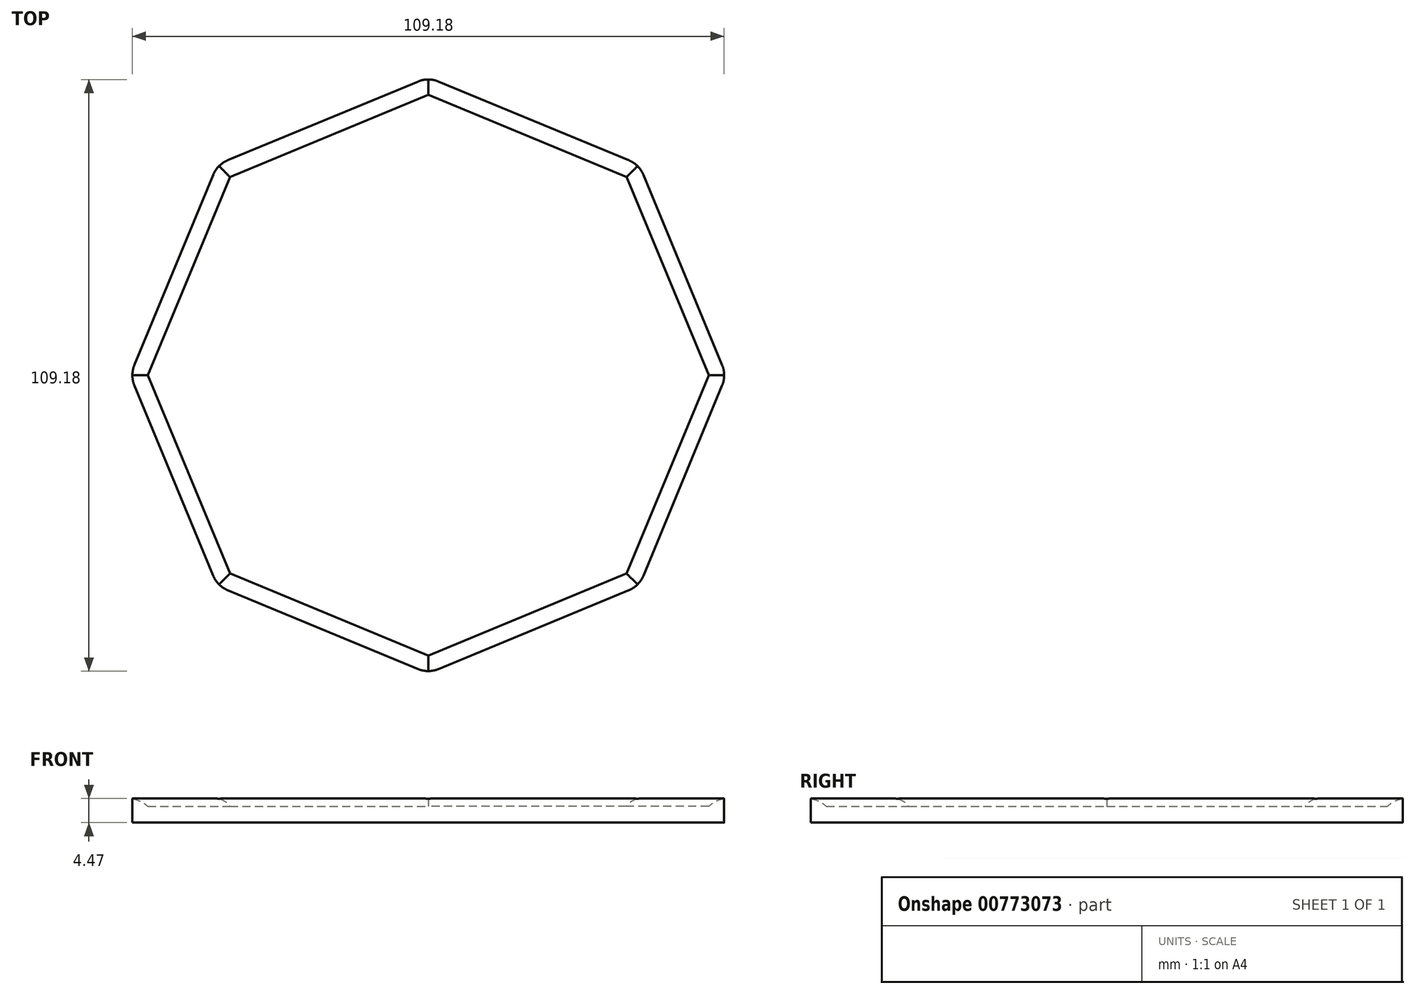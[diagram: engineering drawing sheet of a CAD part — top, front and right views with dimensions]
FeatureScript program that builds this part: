
annotation { "Feature Type Name" : "Feature", "Feature Type Description" : "" }
export const myFeature = defineFeature(function(context is Context, id is Id, definition is map)
    precondition{}
    {
        {
            var Q0;
            Q0=qCreatedBy(makeId("Top.planeOp"),FACE);
            var sketch = newSketch(context, id + "F0", { "sketchPlane" : qUnion([Q0])});
            skCircle(sketch, "E0.cCircle", {"center": v(0, 0) * mm, "radius": 55 * mm, "construction": true});
            skLineSegment(sketch, "E0.0", {"start": v(0, 55) * mm, "end": v(38.9, 38.9) * mm});
            skLineSegment(sketch, "E0.1", {"start": v(38.9, 38.9) * mm, "end": v(55, 0) * mm});
            skLineSegment(sketch, "E0.2", {"start": v(55, 0) * mm, "end": v(38.9, -38.9) * mm});
            skLineSegment(sketch, "E0.3", {"start": v(38.9, -38.9) * mm, "end": v(0, -55) * mm});
            skLineSegment(sketch, "E0.4", {"start": v(0, -55) * mm, "end": v(-38.9, -38.9) * mm});
            skLineSegment(sketch, "E0.5", {"start": v(-38.9, -38.9) * mm, "end": v(-55, 0) * mm});
            skLineSegment(sketch, "E0.6", {"start": v(-55, 0) * mm, "end": v(-38.9, 38.9) * mm});
            skLineSegment(sketch, "E0.7", {"start": v(-38.9, 38.9) * mm, "end": v(0, 55) * mm});
            skSolve(sketch);
        }
        {
            var Q0;
            Q0 = qSketchRegion(id + "F0", true);
            extrude(context, id + "F1", {"entities" : qUnion([Q0]), "depth" : 3 * mm, "offsetDistance" : 25 * mm});
        }
        {
            var Q0;
            Q0=makeQuery(id+"F1.opExtrude","CAP_FACE",FACE,{"disambiguationData":[OSD([sQuery(id+"F0.wireOp",EDGE,"E0.0"),sQuery(id+"F0.wireOp",EDGE,"E0.1"),sQuery(id+"F0.wireOp",EDGE,"E0.2"),sQuery(id+"F0.wireOp",EDGE,"E0.3"),sQuery(id+"F0.wireOp",EDGE,"E0.4"),sQuery(id+"F0.wireOp",EDGE,"E0.5"),sQuery(id+"F0.wireOp",EDGE,"E0.6"),sQuery(id+"F0.wireOp",EDGE,"E0.7")])],"isStart":false});
            var sketch = newSketch(context, id + "F2", { "sketchPlane" : qUnion([Q0])});
            skCircle(sketch, "E1.cCircle", {"center": v(0, 0) * mm, "radius": 51.74 * mm, "construction": true});
            skLineSegment(sketch, "E1.0", {"start": v(0, 51.74) * mm, "end": v(36.59, 36.59) * mm});
            skLineSegment(sketch, "E1.1", {"start": v(36.59, 36.59) * mm, "end": v(51.74, 0) * mm});
            skLineSegment(sketch, "E1.2", {"start": v(51.74, 0) * mm, "end": v(36.59, -36.59) * mm});
            skLineSegment(sketch, "E1.3", {"start": v(36.59, -36.59) * mm, "end": v(0, -51.74) * mm});
            skLineSegment(sketch, "E1.4", {"start": v(0, -51.74) * mm, "end": v(-36.59, -36.59) * mm});
            skLineSegment(sketch, "E1.5", {"start": v(-36.59, -36.59) * mm, "end": v(-51.74, 0) * mm});
            skLineSegment(sketch, "E1.6", {"start": v(-51.74, 0) * mm, "end": v(-36.59, 36.59) * mm});
            skLineSegment(sketch, "E1.7", {"start": v(-36.59, 36.59) * mm, "end": v(0, 51.74) * mm});
            skLineSegment(sketch, "E2.0", {"start": v(-38.9, 38.9) * mm, "end": v(0, 55) * mm});
            skLineSegment(sketch, "E3.0", {"start": v(38.9, 38.9) * mm, "end": v(55, 0) * mm});
            skLineSegment(sketch, "E4.0", {"start": v(55, 0) * mm, "end": v(38.9, -38.9) * mm});
            skLineSegment(sketch, "E5.0", {"start": v(38.9, -38.9) * mm, "end": v(0, -55) * mm});
            skLineSegment(sketch, "E6.0", {"start": v(0, -55) * mm, "end": v(-38.9, -38.9) * mm});
            skLineSegment(sketch, "E7.0.0", {"start": v(0, 55) * mm, "end": v(-38.9, 38.9) * mm});
            skLineSegment(sketch, "E7.0.1", {"start": v(-38.9, 38.9) * mm, "end": v(-55, 0) * mm});
            skLineSegment(sketch, "E7.0.2", {"start": v(-55, 0) * mm, "end": v(-38.9, -38.9) * mm});
            skLineSegment(sketch, "E7.0.3", {"start": v(-38.9, -38.9) * mm, "end": v(0, -55) * mm});
            skLineSegment(sketch, "E7.0.4", {"start": v(0, -55) * mm, "end": v(38.9, -38.9) * mm});
            skLineSegment(sketch, "E7.0.5", {"start": v(38.9, -38.9) * mm, "end": v(55, 0) * mm});
            skLineSegment(sketch, "E7.0.6", {"start": v(55, 0) * mm, "end": v(38.9, 38.9) * mm});
            skLineSegment(sketch, "E7.0.7", {"start": v(38.9, 38.9) * mm, "end": v(0, 55) * mm});
            skSolve(sketch);
        }
        {
            var Q0;
            Q0 = qSketchRegion(id + "F2", true);
            extrude(context, id + "F3", {"entities" : qUnion([Q0]), "operationType" : NewBodyOperationType.ADD, "depth" : 1.5 * mm, "offsetDistance" : 25 * mm});
        }
        {
            var Q0;
            Q0=makeQuery(id+"F3.opExtrude","CAP_EDGE",EDGE,{"disambiguationData":[OSD([sQuery(id+"F2.wireOp",EDGE,"E1.7")])],"isStart":false});
            var Q1;
            Q1=makeQuery(id+"F3.opExtrude","CAP_EDGE",EDGE,{"disambiguationData":[OSD([sQuery(id+"F2.wireOp",EDGE,"E1.6")])],"isStart":false});
            var Q2;
            Q2=makeQuery(id+"F3.opExtrude","CAP_EDGE",EDGE,{"disambiguationData":[OSD([sQuery(id+"F2.wireOp",EDGE,"E1.0")])],"isStart":false});
            var Q3;
            Q3=makeQuery(id+"F3.opExtrude","CAP_EDGE",EDGE,{"disambiguationData":[OSD([sQuery(id+"F2.wireOp",EDGE,"E1.1")])],"isStart":false});
            var Q4;
            Q4=makeQuery(id+"F3.opExtrude","CAP_EDGE",EDGE,{"disambiguationData":[OSD([sQuery(id+"F2.wireOp",EDGE,"E1.2")])],"isStart":false});
            var Q5;
            Q5=makeQuery(id+"F3.opExtrude","CAP_EDGE",EDGE,{"disambiguationData":[OSD([sQuery(id+"F2.wireOp",EDGE,"E1.3")])],"isStart":false});
            var Q6;
            Q6=makeQuery(id+"F3.opExtrude","CAP_EDGE",EDGE,{"disambiguationData":[OSD([sQuery(id+"F2.wireOp",EDGE,"E1.5")])],"isStart":false});
            var Q7;
            Q7=makeQuery(id+"F3.opExtrude","CAP_EDGE",EDGE,{"disambiguationData":[OSD([sQuery(id+"F2.wireOp",EDGE,"E1.4")])],"isStart":false});
            var Q8;
            Q8=makeQuery(id+"F3.boolean.opBoolean","MERGE",EDGE,{"derivedFrom":[makeQuery(id+"F1.opExtrude","SWEPT_EDGE",EDGE,{"disambiguationData":[OSD([sQuery(id+"F0.wireOp",EDGE,"E0.3"),sQuery(id+"F0.wireOp",EDGE,"E0.4")])]}),makeQuery(id+"F3.opExtrude","SWEPT_EDGE",EDGE,{"disambiguationData":[OSD([sQuery(id+"F2.wireOp",EDGE,"E7.0.3"),sQuery(id+"F2.wireOp",EDGE,"E7.0.4")])]})]});
            var Q9;
            Q9=makeQuery(id+"F3.boolean.opBoolean","MERGE",EDGE,{"derivedFrom":[makeQuery(id+"F1.opExtrude","SWEPT_EDGE",EDGE,{"disambiguationData":[OSD([sQuery(id+"F0.wireOp",EDGE,"E0.2"),sQuery(id+"F0.wireOp",EDGE,"E0.3")])]}),makeQuery(id+"F3.opExtrude","SWEPT_EDGE",EDGE,{"disambiguationData":[OSD([sQuery(id+"F2.wireOp",EDGE,"E7.0.4"),sQuery(id+"F2.wireOp",EDGE,"E7.0.5")])]})]});
            var Q10;
            Q10=makeQuery(id+"F3.boolean.opBoolean","MERGE",EDGE,{"derivedFrom":[makeQuery(id+"F1.opExtrude","SWEPT_EDGE",EDGE,{"disambiguationData":[OSD([sQuery(id+"F0.wireOp",EDGE,"E0.4"),sQuery(id+"F0.wireOp",EDGE,"E0.5")])]}),makeQuery(id+"F3.opExtrude","SWEPT_EDGE",EDGE,{"disambiguationData":[OSD([sQuery(id+"F2.wireOp",EDGE,"E7.0.2"),sQuery(id+"F2.wireOp",EDGE,"E7.0.3")])]})]});
            var Q11;
            Q11=makeQuery(id+"F3.boolean.opBoolean","MERGE",EDGE,{"derivedFrom":[makeQuery(id+"F1.opExtrude","SWEPT_EDGE",EDGE,{"disambiguationData":[OSD([sQuery(id+"F0.wireOp",EDGE,"E0.5"),sQuery(id+"F0.wireOp",EDGE,"E0.6")])]}),makeQuery(id+"F3.opExtrude","SWEPT_EDGE",EDGE,{"disambiguationData":[OSD([sQuery(id+"F2.wireOp",EDGE,"E7.0.1"),sQuery(id+"F2.wireOp",EDGE,"E7.0.2")])]})]});
            var Q12;
            Q12=makeQuery(id+"F3.boolean.opBoolean","MERGE",EDGE,{"derivedFrom":[makeQuery(id+"F1.opExtrude","SWEPT_EDGE",EDGE,{"disambiguationData":[OSD([sQuery(id+"F0.wireOp",EDGE,"E0.1"),sQuery(id+"F0.wireOp",EDGE,"E0.2")])]}),makeQuery(id+"F3.opExtrude","SWEPT_EDGE",EDGE,{"disambiguationData":[OSD([sQuery(id+"F2.wireOp",EDGE,"E7.0.5"),sQuery(id+"F2.wireOp",EDGE,"E7.0.6")])]})]});
            var Q13;
            Q13=makeQuery(id+"F3.boolean.opBoolean","MERGE",EDGE,{"derivedFrom":[makeQuery(id+"F1.opExtrude","SWEPT_EDGE",EDGE,{"disambiguationData":[OSD([sQuery(id+"F0.wireOp",EDGE,"E0.0"),sQuery(id+"F0.wireOp",EDGE,"E0.1")])]}),makeQuery(id+"F3.opExtrude","SWEPT_EDGE",EDGE,{"disambiguationData":[OSD([sQuery(id+"F2.wireOp",EDGE,"E7.0.6"),sQuery(id+"F2.wireOp",EDGE,"E7.0.7")])]})]});
            var Q14;
            Q14=makeQuery(id+"F3.boolean.opBoolean","MERGE",EDGE,{"derivedFrom":[makeQuery(id+"F1.opExtrude","SWEPT_EDGE",EDGE,{"disambiguationData":[OSD([sQuery(id+"F0.wireOp",EDGE,"E0.0"),sQuery(id+"F0.wireOp",EDGE,"E0.7")])]}),makeQuery(id+"F3.opExtrude","SWEPT_EDGE",EDGE,{"disambiguationData":[OSD([sQuery(id+"F2.wireOp",EDGE,"E7.0.0"),sQuery(id+"F2.wireOp",EDGE,"E7.0.7")])]})]});
            var Q15;
            Q15=makeQuery(id+"F3.boolean.opBoolean","MERGE",EDGE,{"derivedFrom":[makeQuery(id+"F1.opExtrude","SWEPT_EDGE",EDGE,{"disambiguationData":[OSD([sQuery(id+"F0.wireOp",EDGE,"E0.6"),sQuery(id+"F0.wireOp",EDGE,"E0.7")])]}),makeQuery(id+"F3.opExtrude","SWEPT_EDGE",EDGE,{"disambiguationData":[OSD([sQuery(id+"F2.wireOp",EDGE,"E7.0.0"),sQuery(id+"F2.wireOp",EDGE,"E7.0.1")])]})]});
            fillet(context, id + "F4", {"entities" : qUnion([Q0, Q1, Q2, Q3, Q4, Q5, Q6, Q7, Q8, Q9, Q10, Q11, Q12, Q13, Q14, Q15]), "radius" : 5 * mm, "tangentPropagation" : true, "allowEdgeOverflow" : false});
        }
    });
